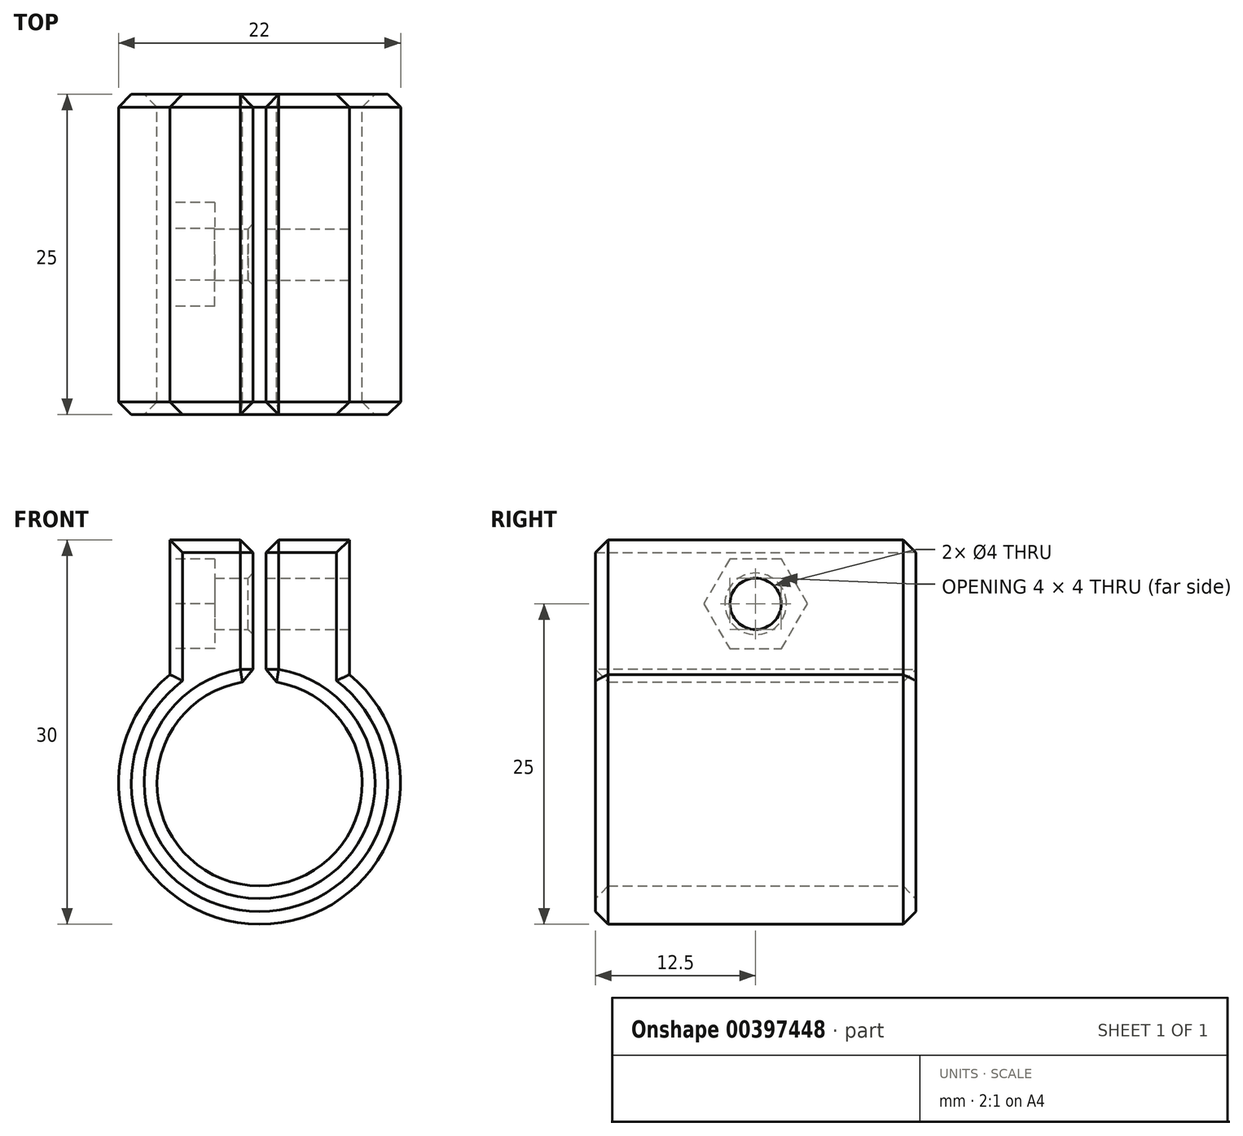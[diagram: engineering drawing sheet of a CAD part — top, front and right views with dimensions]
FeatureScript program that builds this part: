
annotation { "Feature Type Name" : "Feature", "Feature Type Description" : "" }
export const myFeature = defineFeature(function(context is Context, id is Id, definition is map)
    precondition{}
    {
        {
            var Q0;
            Q0=qCreatedBy(makeId("Front.planeOp"),FACE);
            var sketch = newSketch(context, id + "F0", { "sketchPlane" : qUnion([Q0])});
            skCircle(sketch, "E0", {"center": v(0, 0) * mm, "radius": 8 * mm});
            skCircle(sketch, "E1.0", {"center": v(0, 0) * mm, "radius": 11 * mm});
            skLineSegment(sketch, "E2", {"start": v(-7, 8.49) * mm, "end": v(-7, 19) * mm});
            skLineSegment(sketch, "E3", {"start": v(-7, 19) * mm, "end": v(7, 19) * mm});
            skLineSegment(sketch, "E4", {"start": v(7, 19) * mm, "end": v(7, 8.49) * mm});
            skLineSegment(sketch, "E5", {"start": v(-0.5, 19) * mm, "end": v(-0.5, 7.98) * mm});
            skLineSegment(sketch, "E6", {"start": v(0.5, 7.98) * mm, "end": v(0.5, 19) * mm});
            skSolve(sketch);
        }
        {
            var Q0;
            {var subQ0=sQuery(id+"F0.wireOp",EDGE,"E2");Q0=makeQuery(id+"F0.imprint","IMPRINT",FACE,{"disambiguationData":[TD([[makeQuery(id+"F0.imprint","IMPRINT",EDGE,{"derivedFrom":subQ0}),-1.0]])]});}
            var Q1;
            {var subQ0=sQuery(id+"F0.wireOp",EDGE,"E4");Q1=makeQuery(id+"F0.imprint","IMPRINT",FACE,{"disambiguationData":[TD([[makeQuery(id+"F0.imprint","IMPRINT",EDGE,{"derivedFrom":subQ0}),-1.0]])]});}
            var Q2;
            {var subQ3=sQuery(id+"F0.wireOp",EDGE,"E5");var subQ7=sQuery(id+"F0.wireOp",EDGE,"E0");var subQ9=makeQuery(id+"F0.imprint","INTERSECT",VERTEX,{"derivedFrom":[subQ7,subQ3]});Q2=makeQuery(id+"F0.imprint","IMPRINT",FACE,{"disambiguationData":[TD([[makeQuery(id+"F0.imprint","IMPRINT",EDGE,{"disambiguationData":[TD([[subQ9,-1.0]])],"derivedFrom":subQ7}),-1.0]])]});}
            extrude(context, id + "F1", {"entities" : qUnion([Q0, Q1, Q2]), "depth" : 25 * mm});
        }
        {
            var Q0;
            Q0=makeQuery(id+"F1.opExtrude","SWEPT_FACE",FACE,{"disambiguationData":[OSD([sQuery(id+"F0.wireOp",EDGE,"E4")])]});
            var sketch = newSketch(context, id + "F2", { "sketchPlane" : qUnion([Q0])});
            skCircle(sketch, "E7", {"center": v(-12.5, 14) * mm, "radius": 2 * mm});
            skSolve(sketch);
        }
        {
            var Q0;
            Q0=makeQuery(id+"F2.imprint","IMPRINT",FACE,{"disambiguationData":[TD([[makeQuery(id+"F2.imprint","IMPRINT",EDGE,{"derivedFrom":sQuery(id+"F2.wireOp",EDGE,"E7")}),1.0]])]});
            extrude(context, id + "F3", {"entities" : qUnion([Q0]), "operationType" : NewBodyOperationType.REMOVE, "endBound" : BoundingType.THROUGH_ALL, "oppositeDirection" : true, "depth" : 25 * mm});
        }
        {
            var Q0;
            Q0=makeQuery(id+"F1.opExtrude","SWEPT_FACE",FACE,{"disambiguationData":[OSD([sQuery(id+"F0.wireOp",EDGE,"E2")])]});
            var sketch = newSketch(context, id + "F4", { "sketchPlane" : qUnion([Q0])});
            skCircle(sketch, "E8.cCircle", {"center": v(12.5, 14) * mm, "radius": 3.5 * mm, "construction": true});
            skLineSegment(sketch, "E8.0", {"start": v(14.52, 10.5) * mm, "end": v(10.48, 10.5) * mm});
            skLineSegment(sketch, "E8.1", {"start": v(10.48, 10.5) * mm, "end": v(8.46, 14) * mm});
            skLineSegment(sketch, "E8.2", {"start": v(8.46, 14) * mm, "end": v(10.48, 17.5) * mm});
            skLineSegment(sketch, "E8.3", {"start": v(10.48, 17.5) * mm, "end": v(14.52, 17.5) * mm});
            skLineSegment(sketch, "E8.4", {"start": v(14.52, 17.5) * mm, "end": v(16.54, 14) * mm});
            skLineSegment(sketch, "E8.5", {"start": v(16.54, 14) * mm, "end": v(14.52, 10.5) * mm});
            skPoint(sketch, "E8.0.midPoint", {"position": v(12.5, 10.5) * mm});
            skSolve(sketch);
        }
        {
            var Q0;
            Q0=makeQuery(id+"F4.imprint","IMPRINT",FACE,{"disambiguationData":[TD([[makeQuery(id+"F4.imprint","IMPRINT",EDGE,{"derivedFrom":sQuery(id+"F4.wireOp",EDGE,"E8.0")}),-1.0]])]});
            extrude(context, id + "F5", {"entities" : qUnion([Q0]), "operationType" : NewBodyOperationType.REMOVE, "oppositeDirection" : true, "offsetDistance" : 25 * mm, "depth" : 3.5 * mm});
        }
        {
            var Q0;
            Q0=makeQuery(id+"F5.boolean.opBoolean","COPY",EDGE,{"derivedFrom":makeQuery(id+"F5.opExtrude","CAP_EDGE",EDGE,{"disambiguationData":[OSD([sQuery(id+"F4.wireOp",EDGE,"E8.0")])],"isStart":true})});
            var Q1;
            Q1=makeQuery(id+"F5.boolean.opBoolean","COPY",EDGE,{"derivedFrom":makeQuery(id+"F5.opExtrude","CAP_EDGE",EDGE,{"disambiguationData":[OSD([sQuery(id+"F4.wireOp",EDGE,"E8.5")])],"isStart":true})});
            var Q2;
            Q2=makeQuery(id+"F5.boolean.opBoolean","COPY",EDGE,{"derivedFrom":makeQuery(id+"F5.opExtrude","CAP_EDGE",EDGE,{"disambiguationData":[OSD([sQuery(id+"F4.wireOp",EDGE,"E8.4")])],"isStart":true})});
            var Q3;
            Q3=makeQuery(id+"F5.boolean.opBoolean","COPY",EDGE,{"derivedFrom":makeQuery(id+"F5.opExtrude","CAP_EDGE",EDGE,{"disambiguationData":[OSD([sQuery(id+"F4.wireOp",EDGE,"E8.3")])],"isStart":true})});
            var Q4;
            Q4=makeQuery(id+"F5.boolean.opBoolean","COPY",EDGE,{"derivedFrom":makeQuery(id+"F5.opExtrude","CAP_EDGE",EDGE,{"disambiguationData":[OSD([sQuery(id+"F4.wireOp",EDGE,"E8.1")])],"isStart":true})});
            var Q5;
            Q5=makeQuery(id+"F5.boolean.opBoolean","COPY",EDGE,{"derivedFrom":makeQuery(id+"F5.opExtrude","CAP_EDGE",EDGE,{"disambiguationData":[OSD([sQuery(id+"F4.wireOp",EDGE,"E8.2")])],"isStart":true})});
            var Q6;
            Q6=makeQuery(id+"F3.boolean.opBoolean","COPY",EDGE,{"derivedFrom":makeQuery(id+"F3.opExtrude","CAP_EDGE",EDGE,{"disambiguationData":[OSD([sQuery(id+"F2.wireOp",EDGE,"E7")])],"isStart":true})});
            var Q7;
            Q7=makeQuery(id+"F3.boolean.opBoolean","INTERSECT",EDGE,{"derivedFrom":[makeQuery(id+"F1.opExtrude","SWEPT_FACE",FACE,{"disambiguationData":[OSD([sQuery(id+"F0.wireOp",EDGE,"E5")])]}),makeQuery(id+"F3.opExtrude","SWEPT_FACE",FACE,{"disambiguationData":[OSD([sQuery(id+"F2.wireOp",EDGE,"E7")])]})]});
            chamfer(context, id + "F6", {"entities" : qUnion([Q0, Q1, Q2, Q3, Q4, Q5, Q6, Q7]), "width" : .4 * mm, "tangentPropagation" : true});
        }
        {
            var Q0;
            Q0=makeQuery(id+"F1.opExtrude","CAP_FACE",FACE,{"disambiguationData":[OSD([sQuery(id+"F0.wireOp",EDGE,"E0"),sQuery(id+"F0.wireOp",EDGE,"E1.0"),sQuery(id+"F0.wireOp",EDGE,"E2"),sQuery(id+"F0.wireOp",EDGE,"E3"),sQuery(id+"F0.wireOp",EDGE,"E4"),sQuery(id+"F0.wireOp",EDGE,"E5"),sQuery(id+"F0.wireOp",EDGE,"E6")])],"isStart":false});
            var Q1;
            Q1=makeQuery(id+"F1.opExtrude","CAP_FACE",FACE,{"disambiguationData":[OSD([sQuery(id+"F0.wireOp",EDGE,"E0"),sQuery(id+"F0.wireOp",EDGE,"E1.0"),sQuery(id+"F0.wireOp",EDGE,"E2"),sQuery(id+"F0.wireOp",EDGE,"E3"),sQuery(id+"F0.wireOp",EDGE,"E4"),sQuery(id+"F0.wireOp",EDGE,"E5"),sQuery(id+"F0.wireOp",EDGE,"E6")])],"isStart":true});
            var Q2;
            Q2=makeQuery(id+"F1.opExtrude","SWEPT_EDGE",EDGE,{"disambiguationData":[OSD([sQuery(id+"F0.wireOp",EDGE,"E0"),sQuery(id+"F0.wireOp",EDGE,"E5")])]});
            var Q3;
            Q3=makeQuery(id+"F1.opExtrude","SWEPT_EDGE",EDGE,{"disambiguationData":[OSD([sQuery(id+"F0.wireOp",EDGE,"E0"),sQuery(id+"F0.wireOp",EDGE,"E6")])]});
            var Q4;
            Q4=makeQuery(id+"F1.opExtrude","SWEPT_EDGE",EDGE,{"disambiguationData":[OSD([sQuery(id+"F0.wireOp",EDGE,"E3"),sQuery(id+"F0.wireOp",EDGE,"E5")])]});
            var Q5;
            Q5=makeQuery(id+"F1.opExtrude","SWEPT_EDGE",EDGE,{"disambiguationData":[OSD([sQuery(id+"F0.wireOp",EDGE,"E3"),sQuery(id+"F0.wireOp",EDGE,"E6")])]});
            chamfer(context, id + "F7", {"entities" : qUnion([Q0, Q1, Q2, Q3, Q4, Q5]), "width" : 1 * mm, "tangentPropagation" : true});
        }
    });
